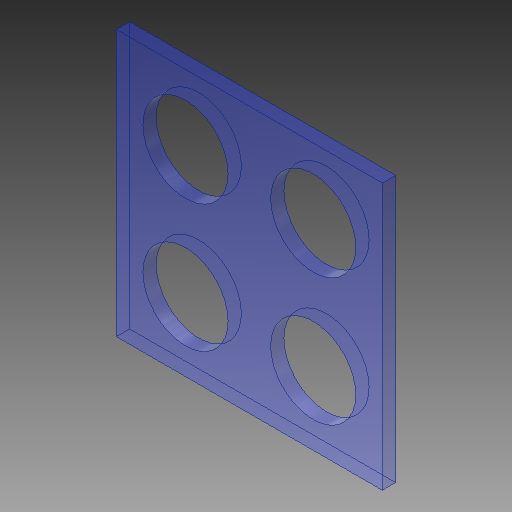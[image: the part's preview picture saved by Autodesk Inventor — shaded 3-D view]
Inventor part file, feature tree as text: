
AUTODESK INVENTOR PART (.ipt)
format: ipt  version: 2018.1 (Build 221171000, 171)  size: 351,232 bytes
history: native  units: mm
features: extrude x2, sketch x2, other x1
ambient origin geometry x8: Origin, YZ Plane, XZ Plane, XY Plane, X Axis, Y Axis, Z Axis, Center Point
bodies: Solid1 (feature_tree)
feature tree (5):
  parser-record x1  (decoder bookkeeping rows leaked as tree rows — omitted from the tree; the rows remain in map.json)
  extrude  "Extrusion1"  Depth=100.0mm
  extrude  "Extrusion3"  TaperAngle=0.0deg  [1 undecoded]
  sketch  "Sketch1"  dims[d0=100.0mm d1=100.0mm]
  sketch  "Sketch2"  dims[d2=5.0mm d3=0.0mm d4=32.0mm d5=32.0mm d6=32.0mm d7=32.0mm d15=26.0mm d16=26.0mm d17=26.0mm d18=26.0mm d19=26.0mm d20=26.0mm d21=26.0mm d22=26.0mm d23=48.0mm d24=48.0mm d25=48.0mm d26=48.0mm d29=5.0mm d30=0.0mm]
note: 1 required parameter value undecoded (feature->parameter linkage not recoverable at this tier; creation-order binding heuristic only, values carry confidence <= 0.55)
note: 1 file-system path scrubbed to <path> (originals preserved in map.json)
